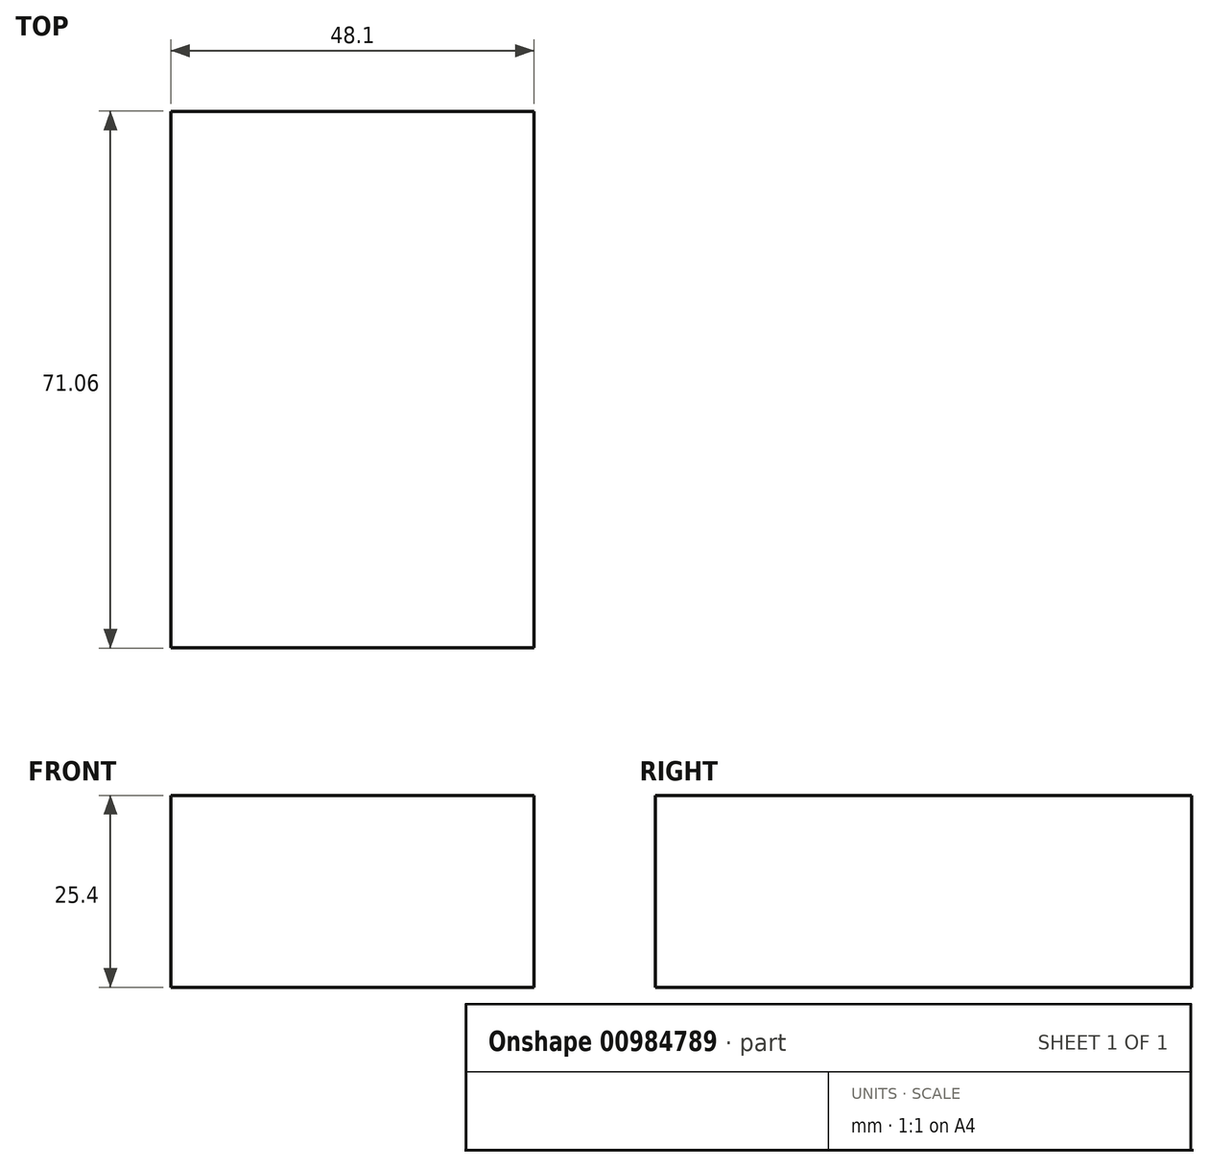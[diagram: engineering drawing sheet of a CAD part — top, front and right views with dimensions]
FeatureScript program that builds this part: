
annotation { "Feature Type Name" : "Feature", "Feature Type Description" : "" }
export const myFeature = defineFeature(function(context is Context, id is Id, definition is map)
    precondition{}
    {
        {
            var Q0;
            Q0=qCreatedBy(makeId("Top.planeOp"),FACE);
            var sketch = newSketch(context, id + "F0", { "sketchPlane" : qUnion([Q0])});
            skLineSegment(sketch, "E0.bottom", {"start": v(24.05, 35.53) * mm, "end": v(-24.05, 35.53) * mm});
            skLineSegment(sketch, "E0.top", {"start": v(24.05, -35.53) * mm, "end": v(-24.05, -35.53) * mm});
            skLineSegment(sketch, "E0.left", {"start": v(24.05, 35.53) * mm, "end": v(24.05, -35.53) * mm});
            skLineSegment(sketch, "E0.right", {"start": v(-24.05, 35.53) * mm, "end": v(-24.05, -35.53) * mm});
            skPoint(sketch, "E0.middle", {"position": v(0, 0) * mm});
            skSolve(sketch);
        }
        {
            var Q0;
            Q0=makeQuery(id+"F0.imprint","IMPRINT",FACE,{"disambiguationData":[TD([[makeQuery(id+"F0.imprint","IMPRINT",EDGE,{"derivedFrom":sQuery(id+"F0.wireOp",EDGE,"E0.bottom")}),1.0]])]});
            extrude(context, id + "F1", {"entities" : qUnion([Q0]), "depth" : 25.4 * mm, "offsetDistance" : 25.4 * mm});
        }
    });
